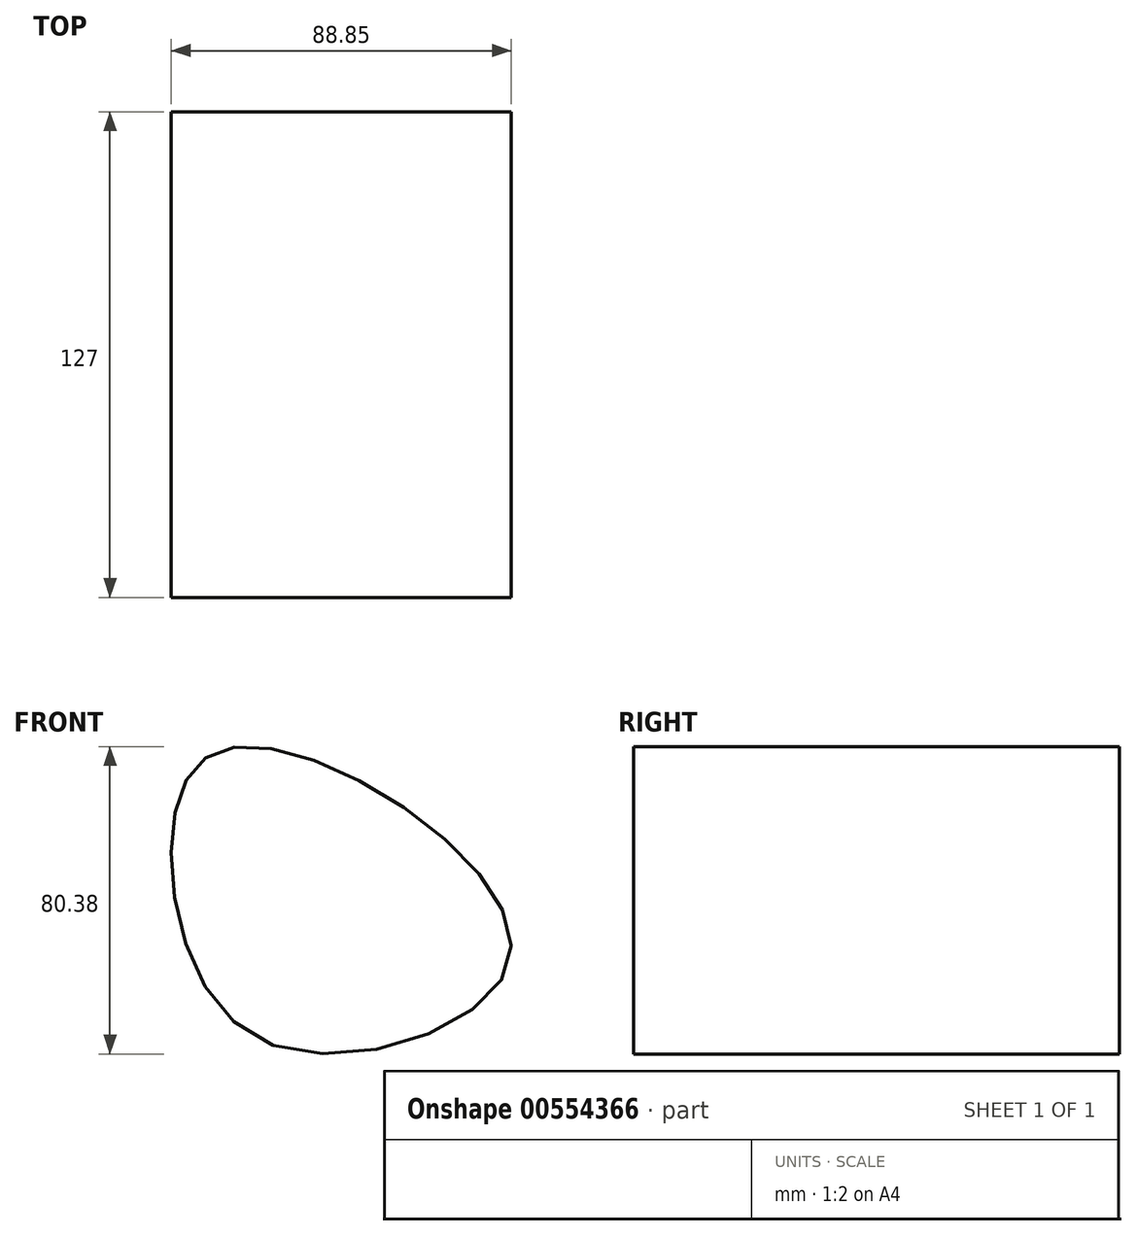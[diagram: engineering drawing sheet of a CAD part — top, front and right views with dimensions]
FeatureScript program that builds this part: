
annotation { "Feature Type Name" : "Feature", "Feature Type Description" : "" }
export const myFeature = defineFeature(function(context is Context, id is Id, definition is map)
    precondition{}
    {
        {
            var Q0;
            Q0=qCreatedBy(makeId("Front.planeOp"),FACE);
            var sketch = newSketch(context, id + "F0", { "sketchPlane" : qUnion([Q0])});
            skFitSpline(sketch, "E0", {"points": [v(-44.5, 23.55) * mm, v(-31.69, 50.2) * mm, v(21.32, 31.62) * mm, v(42.49, -8.57) * mm, v(-19.01, -26.43) * mm, v(-44.5, 23.55) * mm]});
            skSolve(sketch);
        }
        {
            var Q0;
            Q0=makeQuery(id+"F0.imprint","IMPRINT",FACE,{"disambiguationData":[TD([[makeQuery(id+"F0.imprint","IMPRINT",EDGE,{"derivedFrom":sQuery(id+"F0.wireOp",EDGE,"E0")}),-1.0]])]});
            extrude(context, id + "F1", {"entities" : qUnion([Q0]), "depth" : 127 * mm, "offsetDistance" : 25.4 * mm});
        }
    });
